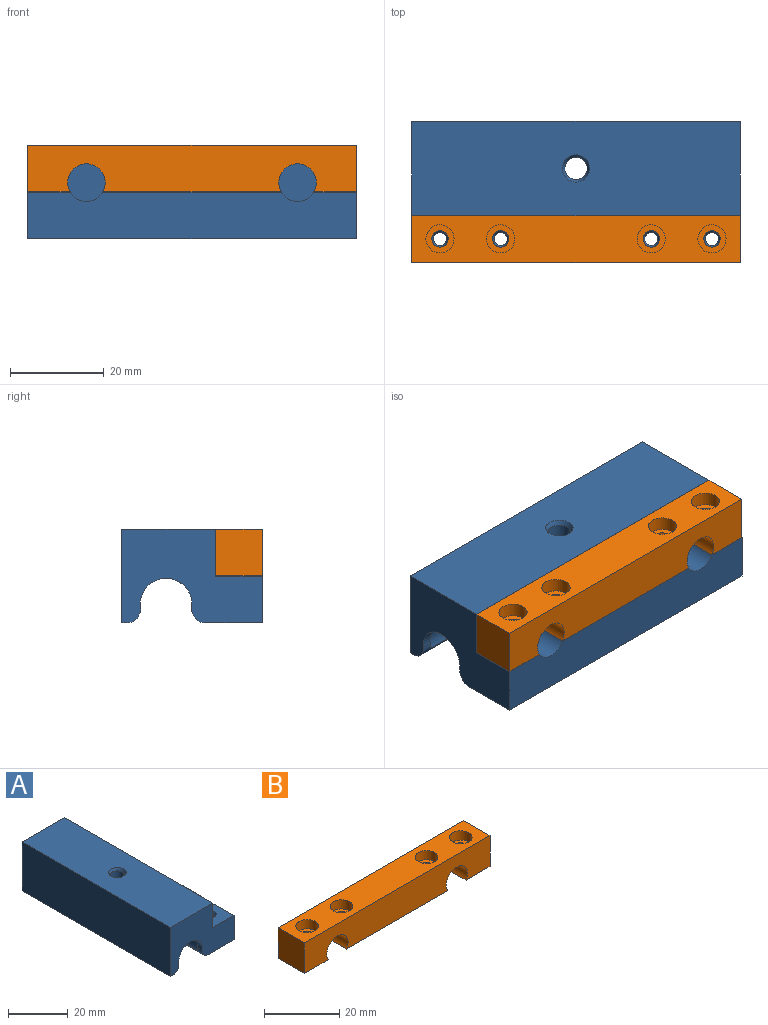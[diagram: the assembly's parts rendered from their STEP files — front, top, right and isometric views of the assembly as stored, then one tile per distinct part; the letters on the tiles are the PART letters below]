
ASSEMBLY  parts=2 mates=1
PART A: 34 faces, bbox 30x70x20 mm
  f0: plane 70x1.05mm, normal (0,0,-1), area 73.5mm2, adj f7,f11,f12,f22
  f1: plane 70x12.07mm, normal (0,0,-1), area 820.1mm2, adj f4,f11,f12,f15,f16,f17,f18,f23
  f2: cylinder r=5.5mm len=25mm, axis (0,-1,0), area 445.8mm2, adj f22,f23,f25,f26,f28
  f3: cylinder r=5.5mm len=11mm, axis (0,-1,0), area 37.2mm2, adj f12,f22,f23,f24
  f4: plane 70x10mm, normal (1,0,0), area 680.3mm2, adj f1,f5,f6,f8,f11,f12,f13,f14
  f5: plane 38.07x10mm, normal (0,0,1), area 358mm2, adj f4,f9,f13,f14,f30,f32
  f6: plane 10x9.04mm, normal (0,0,1), area 79mm2, adj f4,f9,f12,f13,f29
  f7: plane 70x20mm, normal (-1,0,0), area 1400mm2, adj f0,f10,f11,f12
  f8: plane 10x9.04mm, normal (0,0,1), area 79mm2, adj f4,f9,f11,f14,f31
  f9: plane 70x12mm, normal (1,0,0), area 719.7mm2, adj f5,f6,f8,f10,f11,f12,f13,f14
  f10: plane 70x20mm, normal (0,0,1), area 1373.6mm2, adj f7,f9,f11,f12,f33
  f11: plane 30x20mm, normal (0,-1,0), area 405mm2, adj f0,f1,f4,f7,f8,f9,f10,f19
  f12: plane 30x20mm, normal (0,1,0), area 405mm2, adj f0,f1,f3,f4,f6,f7,f9,f10
  f13: cylinder r=4mm len=10mm, axis (1,0,0), area 83.8mm2, adj f4,f5,f6,f9
  f14: cylinder r=4mm len=10mm, axis (1,0,0), area 83.8mm2, adj f4,f5,f8,f9
  f15: cylinder r=1.4mm len=9mm, axis (0,0,1), area 79.2mm2, adj f1,f31
  f16: cylinder r=1.4mm len=9mm, axis (0,0,1), area 79.2mm2, adj f1,f32
  f17: cylinder r=1.4mm len=9mm, axis (0,0,1), area 79.2mm2, adj f1,f30
  f18: cylinder r=1.4mm len=9mm, axis (0,0,1), area 79.2mm2, adj f1,f29
  f19: cylinder r=5.5mm len=11mm, axis (0,-1,0), area 37.2mm2, adj f11,f22,f23,f27
  f20: cylinder r=6mm len=19.5mm, axis (0,-1,0), area 449.6mm2, adj f22,f23,f26,f27
  f21: cylinder r=6mm len=19.5mm, axis (0,1,0), area 449.6mm2, adj f22,f23,f24,f25
  f22: cylinder r=3mm len=70mm, axis (0,-1,0), area 296.6mm2, adj f0,f2,f3,f11,f12,f19,f20,f21
  f23: cylinder r=3mm len=70mm, axis (0,-1,0), area 296.6mm2, adj f1,f2,f3,f11,f12,f19,f20,f21
  f24: cone r=5.5mm half-angle=45deg, axis (0,-1,0), area 15mm2, adj f3,f21,f22,f23
  f25: cone r=6mm half-angle=45deg, axis (0,1,0), area 15mm2, adj f2,f21,f22,f23
  f26: cone r=5.5mm half-angle=45deg, axis (0,-1,0), area 15mm2, adj f2,f20,f22,f23
  f27: cone r=6mm half-angle=45deg, axis (0,1,0), area 15mm2, adj f19,f20,f22,f23
  f28: cylinder r=2.4mm len=10.33mm, axis (0,0,1), area 147.8mm2, adj f2,f33
  f29: cone r=1.4mm half-angle=26.6deg, axis (0,0,1), area 11.6mm2, adj f6,f18
  f30: cone r=1.4mm half-angle=26.6deg, axis (0,0,1), area 11.6mm2, adj f5,f17
  f31: cone r=1.4mm half-angle=26.6deg, axis (0,0,1), area 11.6mm2, adj f8,f15
  f32: cone r=1.4mm half-angle=26.6deg, axis (0,0,1), area 11.6mm2, adj f5,f16
  f33: cone r=2.4mm half-angle=26.6deg, axis (0,0,1), area 18.6mm2, adj f10,f28
PART B: 22 faces, bbox 70x9.9x10 mm
  f0: cylinder r=1.75mm len=7mm, axis (0,0,-1), area 77mm2, adj f9,f20
  f1: cylinder r=1.75mm len=7mm, axis (0,0,-1), area 77mm2, adj f4,f18
  f2: cylinder r=1.75mm len=7mm, axis (0,0,-1), area 77mm2, adj f4,f16
  f3: cylinder r=1.75mm len=7mm, axis (0,0,-1), area 77mm2, adj f5,f14
  f4: plane 38.07x9.9mm, normal (0,0,-1), area 357.7mm2, adj f1,f2,f10,f11,f12,f13
  f5: plane 9.9x9.04mm, normal (0,0,-1), area 79.8mm2, adj f3,f6,f10,f11,f12
  f6: plane 10x9.9mm, normal (1,0,0), area 99mm2, adj f5,f7,f10,f11
  f7: plane 70x9.9mm, normal (0,0,1), area 579.9mm2, adj f6,f8,f10,f11,f15,f17,f19,f21
  f8: plane 10x9.9mm, normal (-1,0,0), area 99mm2, adj f7,f9,f10,f11
  f9: plane 9.9x9.04mm, normal (0,0,-1), area 79.8mm2, adj f0,f8,f10,f11,f13
  f10: plane 70x10mm, normal (0,-1,0), area 619.1mm2, adj f4,f5,f6,f7,f8,f9,f12,f13
  f11: plane 70x10mm, normal (0,1,0), area 619.1mm2, adj f4,f5,f6,f7,f8,f9,f12,f13
  f12: cylinder r=4mm len=9.9mm, axis (0,-1,0), area 165.9mm2, adj f4,f5,f10,f11
  f13: cylinder r=4mm len=9.9mm, axis (0,-1,0), area 165.9mm2, adj f4,f9,f10,f11
  f14: plane 6x6mm, normal (0,0,1), area 18.7mm2, adj f3,f15
  f15: cylinder r=3mm len=6mm, axis (0,0,1), area 56.5mm2, adj f7,f14
  f16: plane 6x6mm, normal (0,0,1), area 18.7mm2, adj f2,f17
  f17: cylinder r=3mm len=6mm, axis (0,0,1), area 56.5mm2, adj f7,f16
  f18: plane 6x6mm, normal (0,0,1), area 18.7mm2, adj f1,f19
  f19: cylinder r=3mm len=6mm, axis (0,0,1), area 56.5mm2, adj f7,f18
  f20: plane 6x6mm, normal (0,0,1), area 18.7mm2, adj f0,f21
  f21: cylinder r=3mm len=6mm, axis (0,0,1), area 56.5mm2, adj f7,f20
PLACE A rot(axis=(0,0,-1),90deg) t=(36.56,44.31,-19.87)mm
PLACE B t=(36.56,19.31,-4.87)mm
MATE fastened A.f15 <-> B.f0  axis (0,0,1) through (7.6,19.31,-9.87)mm
